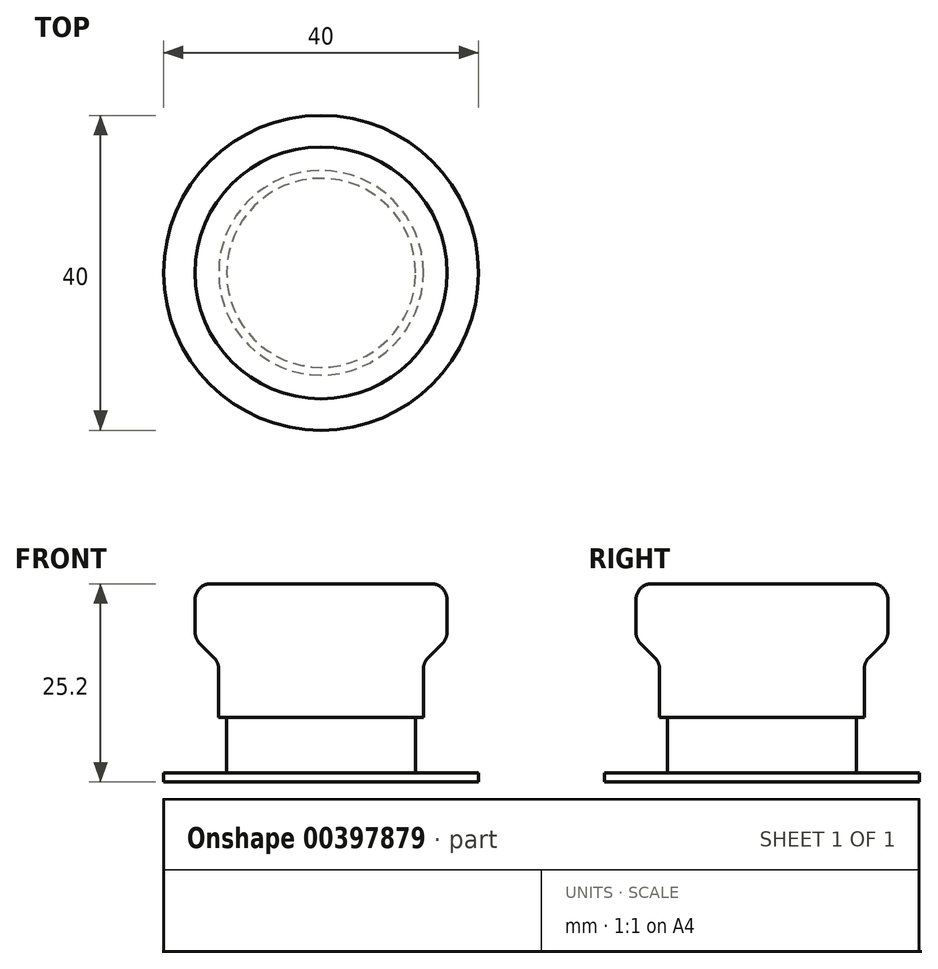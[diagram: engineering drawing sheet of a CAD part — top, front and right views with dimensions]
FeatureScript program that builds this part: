
annotation { "Feature Type Name" : "Feature", "Feature Type Description" : "" }
export const myFeature = defineFeature(function(context is Context, id is Id, definition is map)
    precondition{}
    {
        {
            var Q0;
            Q0=qCreatedBy(makeId("Top.planeOp"),FACE);
            var sketch = newSketch(context, id + "F0", { "sketchPlane" : qUnion([Q0])});
            skCircle(sketch, "E0", {"center": v(0, 0) * mm, "radius": 13 * mm});
            skSolve(sketch);
        }
        {
            var Q0;
            Q0 = qSketchRegion(id + "F0", true);
            extrude(context, id + "F1", {"entities" : qUnion([Q0]), "depth" : 7 * mm});
        }
        {
            var Q0;
            Q0=makeQuery(id+"F1.opExtrude","CAP_FACE",FACE,{"disambiguationData":[OSD([sQuery(id+"F0.wireOp",EDGE,"E0")])],"isStart":false});
            var sketch = newSketch(context, id + "F2", { "sketchPlane" : qUnion([Q0])});
            skCircle(sketch, "E1", {"center": v(0, 0) * mm, "radius": 16 * mm});
            skSolve(sketch);
        }
        {
            var Q0;
            Q0 = qSketchRegion(id + "F2", true);
            extrude(context, id + "F3", {"entities" : qUnion([Q0]), "operationType" : NewBodyOperationType.ADD, "depth" : 10 * mm});
        }
        {
            var Q0;
            Q0=makeQuery(id+"F3.opExtrude","CAP_EDGE",EDGE,{"disambiguationData":[OSD([sQuery(id+"F2.wireOp",EDGE,"E1")])],"isStart":true});
            chamfer(context, id + "F4", {"entities" : qUnion([Q0]), "width" : 3 * mm, "tangentPropagation" : true});
        }
        {
            var Q0;
            Q0=makeQuery(id+"F4.opChamfer","BLEND_EDGE",EDGE,{"blendedFrom":[makeQuery(id+"F3.opExtrude","CAP_EDGE",EDGE,{"disambiguationData":[OSD([sQuery(id+"F2.wireOp",EDGE,"E1")])],"isStart":true}),makeQuery(id+"F1.opExtrude","SWEPT_FACE",FACE,{"disambiguationData":[OSD([sQuery(id+"F0.wireOp",EDGE,"E0")])]})],"blendedInto":[makeQuery(id+"F1.opExtrude","SWEPT_FACE",FACE,{"disambiguationData":[OSD([sQuery(id+"F0.wireOp",EDGE,"E0")])]})]});
            var Q1;
            {var subQ0=sQuery(id+"F2.wireOp",EDGE,"E1");Q1=makeQuery(id+"F4.opChamfer","BLEND_EDGE",EDGE,{"blendedFrom":[makeQuery(id+"F3.opExtrude","CAP_EDGE",EDGE,{"disambiguationData":[OSD([subQ0])],"isStart":true}),makeQuery(id+"F3.opExtrude","SWEPT_FACE",FACE,{"disambiguationData":[OSD([subQ0])]})],"blendedInto":[makeQuery(id+"F3.opExtrude","SWEPT_FACE",FACE,{"disambiguationData":[OSD([subQ0])]})]});}
            var Q2;
            Q2=makeQuery(id+"F3.opExtrude","CAP_EDGE",EDGE,{"disambiguationData":[OSD([sQuery(id+"F2.wireOp",EDGE,"E1")])],"isStart":false});
            fillet(context, id + "F5", {"entities" : qUnion([Q0, Q1, Q2]), "radius" : 2 * mm, "tangentPropagation" : true, "allowEdgeOverflow" : false});
        }
        {
            var Q0;
            Q0=makeQuery(id+"F1.opExtrude","CAP_FACE",FACE,{"disambiguationData":[OSD([sQuery(id+"F0.wireOp",EDGE,"E0")])],"isStart":true});
            var sketch = newSketch(context, id + "F6", { "sketchPlane" : qUnion([Q0])});
            skCircle(sketch, "E2", {"center": v(0, 0) * mm, "radius": 12 * mm});
            skSolve(sketch);
        }
        {
            var Q0;
            Q0 = qSketchRegion(id + "F6", true);
            extrude(context, id + "F7", {"entities" : qUnion([Q0]), "depth" : 7 * mm});
        }
        {
            var Q0;
            Q0=makeQuery(id+"F7.opExtrude","CAP_FACE",FACE,{"disambiguationData":[OSD([sQuery(id+"F6.wireOp",EDGE,"E2")])],"isStart":false});
            var sketch = newSketch(context, id + "F8", { "sketchPlane" : qUnion([Q0])});
            skCircle(sketch, "E3", {"center": v(0, 0) * mm, "radius": 20 * mm});
            skSolve(sketch);
        }
        {
            var Q0;
            Q0 = qSketchRegion(id + "F8", true);
            extrude(context, id + "F9", {"entities" : qUnion([Q0]), "depth" : 1.2 * mm});
        }
    });
